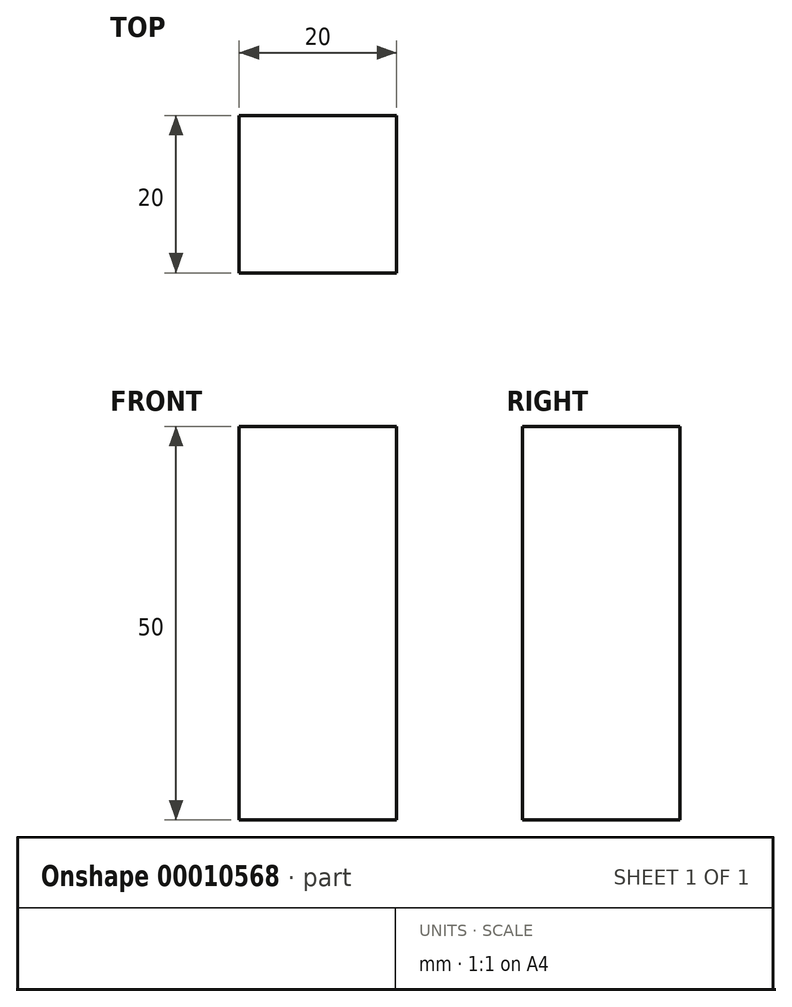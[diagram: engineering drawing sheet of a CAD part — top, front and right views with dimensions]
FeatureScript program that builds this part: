
annotation { "Feature Type Name" : "Feature", "Feature Type Description" : "" }
export const myFeature = defineFeature(function(context is Context, id is Id, definition is map)
    precondition{}
    {
        {
            var Q0;
            Q0=qCreatedBy(makeId("Front.planeOp"),FACE);
            var sketch = newSketch(context, id + "F0", { "sketchPlane" : qUnion([Q0])});
            skLineSegment(sketch, "E0.bottom", {"start": v(-10, 14.62) * mm, "end": v(10, 14.62) * mm});
            skLineSegment(sketch, "E0.top", {"start": v(-10, -35.38) * mm, "end": v(10, -35.38) * mm});
            skLineSegment(sketch, "E0.left", {"start": v(-10, 14.62) * mm, "end": v(-10, -35.38) * mm});
            skLineSegment(sketch, "E0.right", {"start": v(10, 14.62) * mm, "end": v(10, -35.38) * mm});
            skSolve(sketch);
        }
        {
            var Q0;
            Q0=makeQuery(id+"F0.imprint","IMPRINT",FACE,{"disambiguationData":[TD([[makeQuery(id+"F0.imprint","IMPRINT",EDGE,{"derivedFrom":sQuery(id+"F0.wireOp",EDGE,"E0.bottom")}),-1.0]])]});
            extrude(context, id + "F1", {"entities" : qUnion([Q0]), "depth" : 20 * mm});
        }
        {
            var Q0;
            Q0=makeQuery(id+"F1.opExtrude","CAP_FACE",FACE,{"disambiguationData":[OSD([sQuery(id+"F0.wireOp",EDGE,"E0.bottom"),sQuery(id+"F0.wireOp",EDGE,"E0.top"),sQuery(id+"F0.wireOp",EDGE,"E0.left"),sQuery(id+"F0.wireOp",EDGE,"E0.right")])],"isStart":false});
            var sketch = newSketch(context, id + "F2", { "sketchPlane" : qUnion([Q0])});
            skArc(sketch, "E1", {"start": v(-5, 14.62) * mm, "mid": v(0, 9.62) * mm, "end": v(5, 14.62) * mm});
            skSolve(sketch);
        }
        {
            var Q0;
            Q0=sQuery(id+"F2.wireOp",EDGE,"E1");
            extrude(context, id + "F3", {"bodyType" : ToolBodyType.SURFACE, "surfaceEntities" : qUnion([Q0]), "oppositeDirection" : true, "depth" : 20 * mm});
        }
    });
